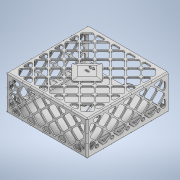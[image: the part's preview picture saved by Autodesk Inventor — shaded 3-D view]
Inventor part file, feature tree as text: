
AUTODESK INVENTOR PART (.ipt)
format: ipt  version: 2020 (Build 240168000, 168)  size: 1,358,336 bytes
history: native  units: in
note: dims shown in document units (in); Inventor stores cm internally (conversion verified against a paired STEP export)
features: other x6, extrude x2, sketch x2
ambient origin geometry x8: Origin, YZ Plane, XZ Plane, XY Plane, X Axis, Y Axis, Z Axis, Center Point
bodies: Solid1 (feature_tree), Solid2 (feature_tree), Solid3 (feature_tree), Solid4 (feature_tree), Solid5 (feature_tree)
feature tree (10):
  other  "Model.iam"
  other  "All.ipt:1"
  other  "Face.ipt:1"
  other  "Side L.ipt:1"
  other  "Side R.ipt:1"
  other  "Back.ipt:1"
  extrude  "Extrusion1"  Depth=0.3937in TaperAngle=0.0deg
  extrude  "Extrusion2"  [1 undecoded]
  sketch  "Sketch1"  dims[d0=0.3937in d1=1.0in d2=0.0in]
  sketch  "Sketch2"  dims[d3=1.0in d4=0.0in]
note: 1 required parameter value undecoded (feature->parameter linkage not recoverable at this tier; creation-order binding heuristic only, values carry confidence <= 0.55)
